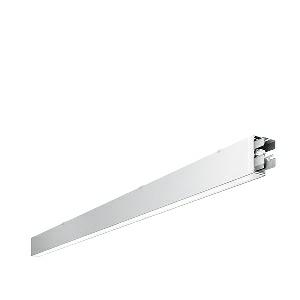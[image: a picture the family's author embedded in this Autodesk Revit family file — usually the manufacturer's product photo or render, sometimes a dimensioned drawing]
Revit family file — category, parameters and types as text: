
# Revit family: dotoo_line_-_dla_3000_840_d_sta_00807934_8d48
name_source: partatom
category: Lighting Fixtures
units: mm (PartAtom-declared; Revit-internal decimal feet)

## family parameters
Cut with Voids When Loaded = No
Host = Face
Light Source = No
Part Type = Normal
Room Calculation Point = No
Round Connector Dimension = Use Diameter
Shared = No

## types (1)
- DOTOO.line - DLA 3000/840/D STA (1 x LED, 2750 lm, 4000K)
    Apparent Load = 26 VA
    Approval mark = CE
    CIE Flux Codes = 67 91 98 100 100
    Color Rendering = 80-89
    Color Temperature = 4000K
    Control Gear = Electronic ballast
    Default Elevation = 1800 mm
    Description = DLA 3000/840/D|Surface-mounted luminaire.|light source: LED|work equipment: Adjustable electronic ballast, digital DALI|connected load: 220-240 V, 50/60 Hz|Power consumption: approx. 26 W|luminous flux: 2750 lm|luminous efficacy: 105 lm/W|light distribution: Direct|colour temperature: Cold white, ca. 4000 K|class of protection: I|technology: Continuously dimmable|mains lead: Connector|glare control: Prism aperture|special features: DALI Load 1x, TouchDIM - dimming via standard switch, Through-wired, up to 18 m on one mains connection, Flicker-free, Suitable as emergency lighting, Start luminaire with mains connection, Mechanical and electrical connection of the individual modules without tools|
    Frequency = 50 Hz
    Height = 110 mm
    Lamp = 1 x LED
    Lamp Light Flux = 2750 lm
    Lamp count = 1
    Length = 2250 mm
    Luminous efficacy = 106 lm/W
    Manufacturer = Waldmann
    ModVariant = No
    Model = 00807934
    Mounting Place = Ceiling
    Mounting Type = Surface mounted
    Number of Poles = 1
    OnlyDefault = Yes
    Power Factor = 1
    Product Name = DOTOO.line - DLA 3000/840/D STA
    Product group = Ceiling mounted luminaire
    ProductGroupID = 3
    Protection Class = Protection class I
    Protection Degree = IP 40
    RLX_Detail_Level = 1
    RLX_Emergency_Light_Flux = 0 lm
    RLX_Emergency_Type = 0
    RLX_Emergency_Type_DB = No
    RlxData = <blob elided: 20493 chars, md5=8133468c>
    Socket = socket
    Standby Power = 0 W
    System Light Flux = 2750 lm
    System Power = 26 W
    Type Comments = Product without accessories
    Type Image = 114357000-00807934.jpg
    URL = http://relux.com
    VarID = ---
    Voltage = 230 V
    Voltage Range = 220-240 V
    Weight = 0.00 kg
    Width = 60 mm  [stored 0.19685 ft]

note: [stored X ft] marks values corroborated as IEEE doubles in the binary element streams (Revit-internal decimal feet)

## geometry (parser evidence)
native form markers: Blend x4, Sweep x11
no freeform markers — native parametric forms only
